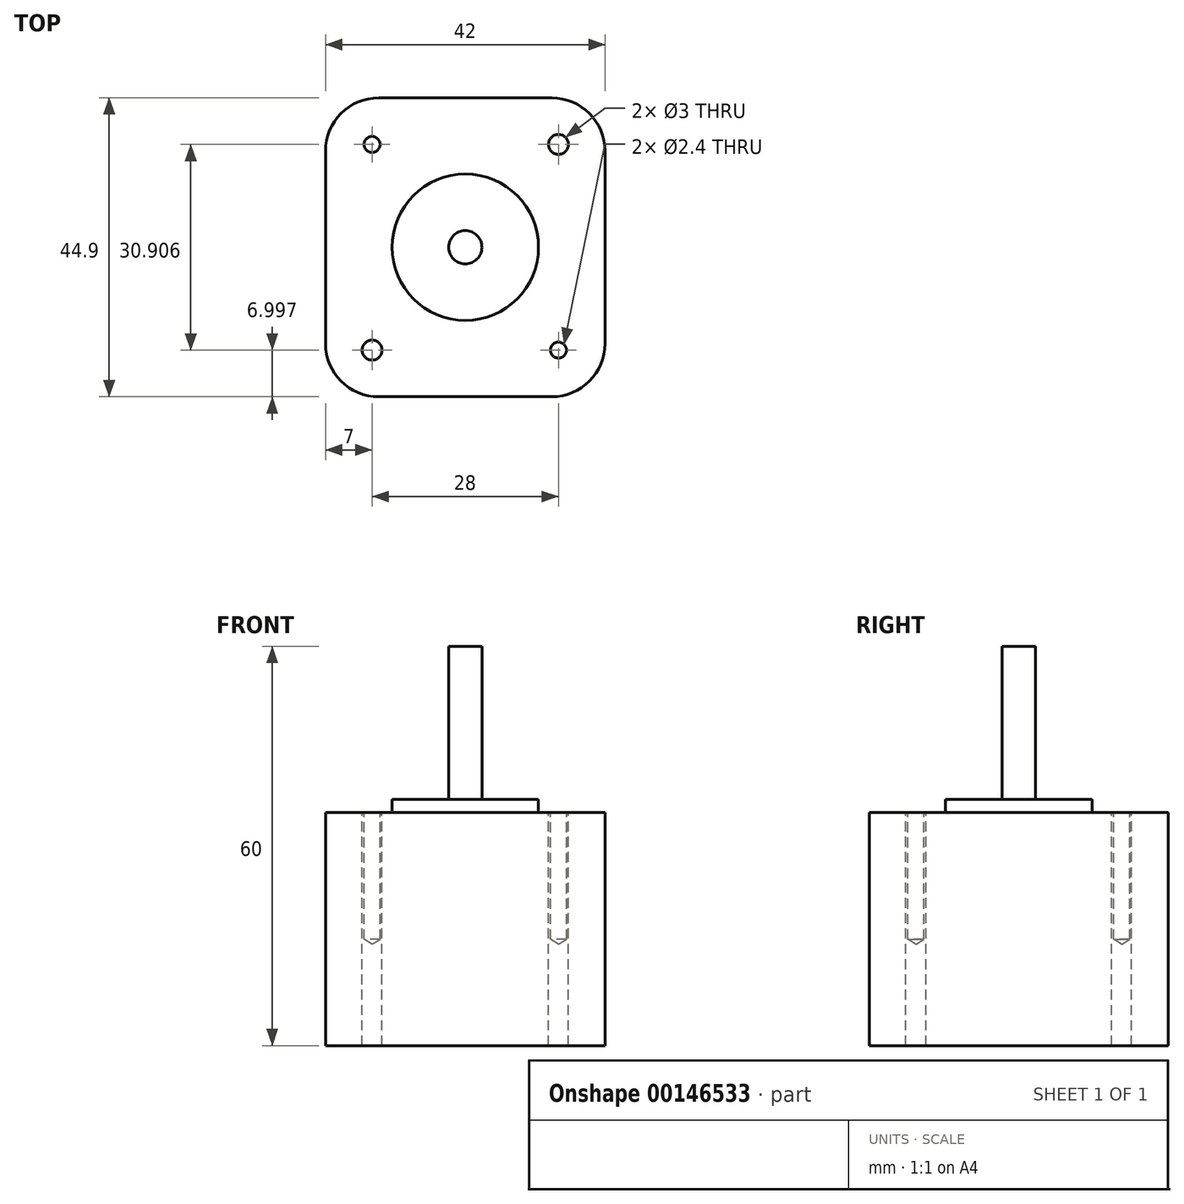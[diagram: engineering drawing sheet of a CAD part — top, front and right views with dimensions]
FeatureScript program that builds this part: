
annotation { "Feature Type Name" : "Feature", "Feature Type Description" : "" }
export const myFeature = defineFeature(function(context is Context, id is Id, definition is map)
    precondition{}
    {
        {
            var Q0;
            Q0=qCreatedBy(makeId("Top.planeOp"),FACE);
            var sketch = newSketch(context, id + "F0", { "sketchPlane" : qUnion([Q0])});
            skLineSegment(sketch, "E0.bottom", {"start": v(21, -22.45) * mm, "end": v(-21, -22.45) * mm});
            skLineSegment(sketch, "E0.top", {"start": v(21, 22.45) * mm, "end": v(-21, 22.45) * mm});
            skLineSegment(sketch, "E0.left", {"start": v(21, -22.45) * mm, "end": v(21, 22.45) * mm});
            skLineSegment(sketch, "E0.right", {"start": v(-21, -22.45) * mm, "end": v(-21, 22.45) * mm});
            skPoint(sketch, "E0.middle", {"position": v(0, 0) * mm});
            skCircle(sketch, "E1", {"center": v(0, 0) * mm, "radius": 11 * mm});
            skCircle(sketch, "E2", {"center": v(0, 0) * mm, "radius": 2.5 * mm});
            skCircle(sketch, "E3", {"center": v(-14, 15.45) * mm, "radius": 1.5 * mm});
            skLineSegment(sketch, "E4", {"start": v(-21, 22.45) * mm, "end": v(-14, 15.45) * mm, "construction": true});
            skCircle(sketch, "E5.MirrorC", {"center": v(14, 15.45) * mm, "radius": 1.5 * mm});
            skCircle(sketch, "E6.MirrorC", {"center": v(-14, -15.45) * mm, "radius": 1.5 * mm});
            skCircle(sketch, "E7.MirrorC", {"center": v(14, -15.45) * mm, "radius": 1.5 * mm});
            skSolve(sketch);
        }
        {
            var Q0;
            Q0=makeQuery(id+"F0.imprint","IMPRINT",FACE,{"disambiguationData":[TD([[makeQuery(id+"F0.imprint","IMPRINT",EDGE,{"derivedFrom":sQuery(id+"F0.wireOp",EDGE,"E0.bottom")}),-1.0]])]});
            var Q1;
            Q1=makeQuery(id+"F0.imprint","IMPRINT",FACE,{"disambiguationData":[TD([[makeQuery(id+"F0.imprint","IMPRINT",EDGE,{"derivedFrom":sQuery(id+"F0.wireOp",EDGE,"E6.MirrorC")}),-1.0]])]});
            var Q2;
            Q2=makeQuery(id+"F0.imprint","IMPRINT",FACE,{"disambiguationData":[TD([[makeQuery(id+"F0.imprint","IMPRINT",EDGE,{"derivedFrom":sQuery(id+"F0.wireOp",EDGE,"E1")}),1.0]])]});
            var Q3;
            Q3=makeQuery(id+"F0.imprint","IMPRINT",FACE,{"disambiguationData":[TD([[makeQuery(id+"F0.imprint","IMPRINT",EDGE,{"derivedFrom":sQuery(id+"F0.wireOp",EDGE,"E2")}),1.0]])]});
            var Q4;
            Q4=makeQuery(id+"F0.imprint","IMPRINT",FACE,{"disambiguationData":[TD([[makeQuery(id+"F0.imprint","IMPRINT",EDGE,{"derivedFrom":sQuery(id+"F0.wireOp",EDGE,"E7.MirrorC")}),1.0]])]});
            var Q5;
            Q5=makeQuery(id+"F0.imprint","IMPRINT",FACE,{"disambiguationData":[TD([[makeQuery(id+"F0.imprint","IMPRINT",EDGE,{"derivedFrom":sQuery(id+"F0.wireOp",EDGE,"E3")}),1.0]])]});
            var Q6;
            Q6=makeQuery(id+"F0.imprint","IMPRINT",FACE,{"disambiguationData":[TD([[makeQuery(id+"F0.imprint","IMPRINT",EDGE,{"derivedFrom":sQuery(id+"F0.wireOp",EDGE,"E5.MirrorC")}),-1.0]])]});
            extrude(context, id + "F1", {"entities" : qUnion([Q0, Q1, Q2, Q3, Q4, Q5, Q6]), "oppositeDirection" : true, "depth" : 35 * mm});
        }
        {
            var Q0;
            Q0=makeQuery(id+"F0.imprint","IMPRINT",FACE,{"disambiguationData":[TD([[makeQuery(id+"F0.imprint","IMPRINT",EDGE,{"derivedFrom":sQuery(id+"F0.wireOp",EDGE,"E1")}),1.0]])]});
            var Q1;
            Q1=makeQuery(id+"F0.imprint","IMPRINT",FACE,{"disambiguationData":[TD([[makeQuery(id+"F0.imprint","IMPRINT",EDGE,{"derivedFrom":sQuery(id+"F0.wireOp",EDGE,"E2")}),1.0]])]});
            extrude(context, id + "F2", {"entities" : qUnion([Q0, Q1]), "operationType" : NewBodyOperationType.ADD, "depth" : 2 * mm});
        }
        {
            var Q0;
            Q0=makeQuery(id+"F0.imprint","IMPRINT",FACE,{"disambiguationData":[TD([[makeQuery(id+"F0.imprint","IMPRINT",EDGE,{"derivedFrom":sQuery(id+"F0.wireOp",EDGE,"E2")}),1.0]])]});
            extrude(context, id + "F3", {"entities" : qUnion([Q0]), "operationType" : NewBodyOperationType.ADD, "depth" : 25 * mm});
        }
        {
            var Q0;
            Q0=sQuery(id+"F0.wireOp",VERTEX,"E4.end");
            var Q1;
            Q1=sQuery(id+"F0.wireOp",VERTEX,"E5.MirrorC.center");
            var Q2;
            Q2=sQuery(id+"F0.wireOp",VERTEX,"E7.MirrorC.center");
            var Q3;
            Q3=sQuery(id+"F0.wireOp",VERTEX,"E6.MirrorC.center");
            var Q4;
            Q4=makeQuery(id+"F1.opExtrude","SWEPT_BODY",BODY,{"disambiguationData":[OSD([sQuery(id+"F0.wireOp",EDGE,"E0.bottom"),sQuery(id+"F0.wireOp",EDGE,"E0.top"),sQuery(id+"F0.wireOp",EDGE,"E0.left"),sQuery(id+"F0.wireOp",EDGE,"E0.right")])]});
            hole(context, id + "F4", {"style" : HoleStyle.SIMPLE, "endStyle" : HoleEndStyle.BLIND, "standardTappedOrClearance" : lookupTablePath({ "standard" : "ISO", "engagement" : "75%", "pitch" : "0.6 mm", "size" : "M3", "type" : "Tapped" }), "standardBlindInLast" : lookupTablePath({ "standard" : "ISO", "engagement" : "75%", "pitch" : "0.6 mm", "size" : "M3", "type" : "Tapped" }), "holeDiameter" : 2.4 * mm, "holeDepth" : 19.05 * mm, "startFromSketch" : true, "locations" : qUnion([Q0, Q1, Q2, Q3]), "scope" : qUnion([Q4])});
        }
        {
            var Q0;
            Q0=makeQuery(id+"F1.opExtrude","SWEPT_EDGE",EDGE,{"disambiguationData":[OSD([sQuery(id+"F0.wireOp",EDGE,"E0.top"),sQuery(id+"F0.wireOp",EDGE,"E0.left")])]});
            var Q1;
            Q1=makeQuery(id+"F1.opExtrude","SWEPT_EDGE",EDGE,{"disambiguationData":[OSD([sQuery(id+"F0.wireOp",EDGE,"E0.bottom"),sQuery(id+"F0.wireOp",EDGE,"E0.left")])]});
            var Q2;
            Q2=makeQuery(id+"F1.opExtrude","SWEPT_EDGE",EDGE,{"disambiguationData":[OSD([sQuery(id+"F0.wireOp",EDGE,"E0.top"),sQuery(id+"F0.wireOp",EDGE,"E0.right")])]});
            var Q3;
            Q3=makeQuery(id+"F1.opExtrude","SWEPT_EDGE",EDGE,{"disambiguationData":[OSD([sQuery(id+"F0.wireOp",EDGE,"E0.bottom"),sQuery(id+"F0.wireOp",EDGE,"E0.right")])]});
            fillet(context, id + "F5", {"entities" : qUnion([Q0, Q1, Q2, Q3]), "radius" : 8 * mm, "tangentPropagation" : true, "allowEdgeOverflow" : false});
        }
    });
